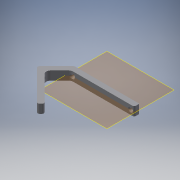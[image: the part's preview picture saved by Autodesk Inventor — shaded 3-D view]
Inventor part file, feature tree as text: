
AUTODESK INVENTOR PART (.ipt)
format: ipt  version: 2019 (Build 230136000, 136)  size: 212,992 bytes
history: native  units: mm
features: fillet x5, sketch x3, extrude x3, chamfer x2, plane x1
ambient origin geometry x8: Origin, YZ Plane, XZ Plane, XY Plane, X Axis, Y Axis, Z Axis, Center Point
bodies: Solid1 (feature_tree)
feature tree (14):
  sketch  "Sketch1"  dims[d0=66.0mm d1=90.0mm d2=3.4mm d3=3.4mm d4=45.0mm d5=37.0mm d6=37.0mm]
  plane  "Work Plane1"
  extrude  "Extrusion1"  Depth=90.0mm
  fillet  "Fillet1"  Radius=3.4mm
  fillet  "Fillet2"  Radius=3.4mm
  fillet  "Fillet3"  Radius=45.0mm
  fillet  "Fillet4"  Radius=37.0mm
  fillet  "Fillet5"  Radius=37.0mm
  extrude  "Extrusion2"  TaperAngle=135.0deg  [1 undecoded]
  extrude  "Extrusion3"  TaperAngle=135.0deg  [1 undecoded]
  chamfer  "Chamfer1"  Angle=45.0deg  [1 undecoded]
  chamfer  "Chamfer2"  Distance=6.0mm
  sketch  "Sketch2"  dims[d7=30.0mm d8=135.0deg]
  sketch  "Sketch3"  dims[d9=100.0mm d10=135.0deg d11=45.0deg d13=6.0mm d14=6.0mm d15=135.0deg d16=14.451339mm d17=6.0mm d18=20.162951mm d19=15.213203mm d20=10.0mm d21=0.0mm d22=5.0mm d23=0.5mm d24=2.0mm d25=2.0mm d26=2.0mm d27=10.0mm d28=0.0mm d29=180.0deg d30=30.0mm d31=3.5mm d32=3.5mm d33=10.0mm d34=0.0mm d35=1.0mm d36=2.0mm d37=45.0deg d38=1.0mm d39=2.0mm d40=45.0deg]
note: 3 required parameter values undecoded (feature->parameter linkage not recoverable at this tier; creation-order binding heuristic only, values carry confidence <= 0.55)
